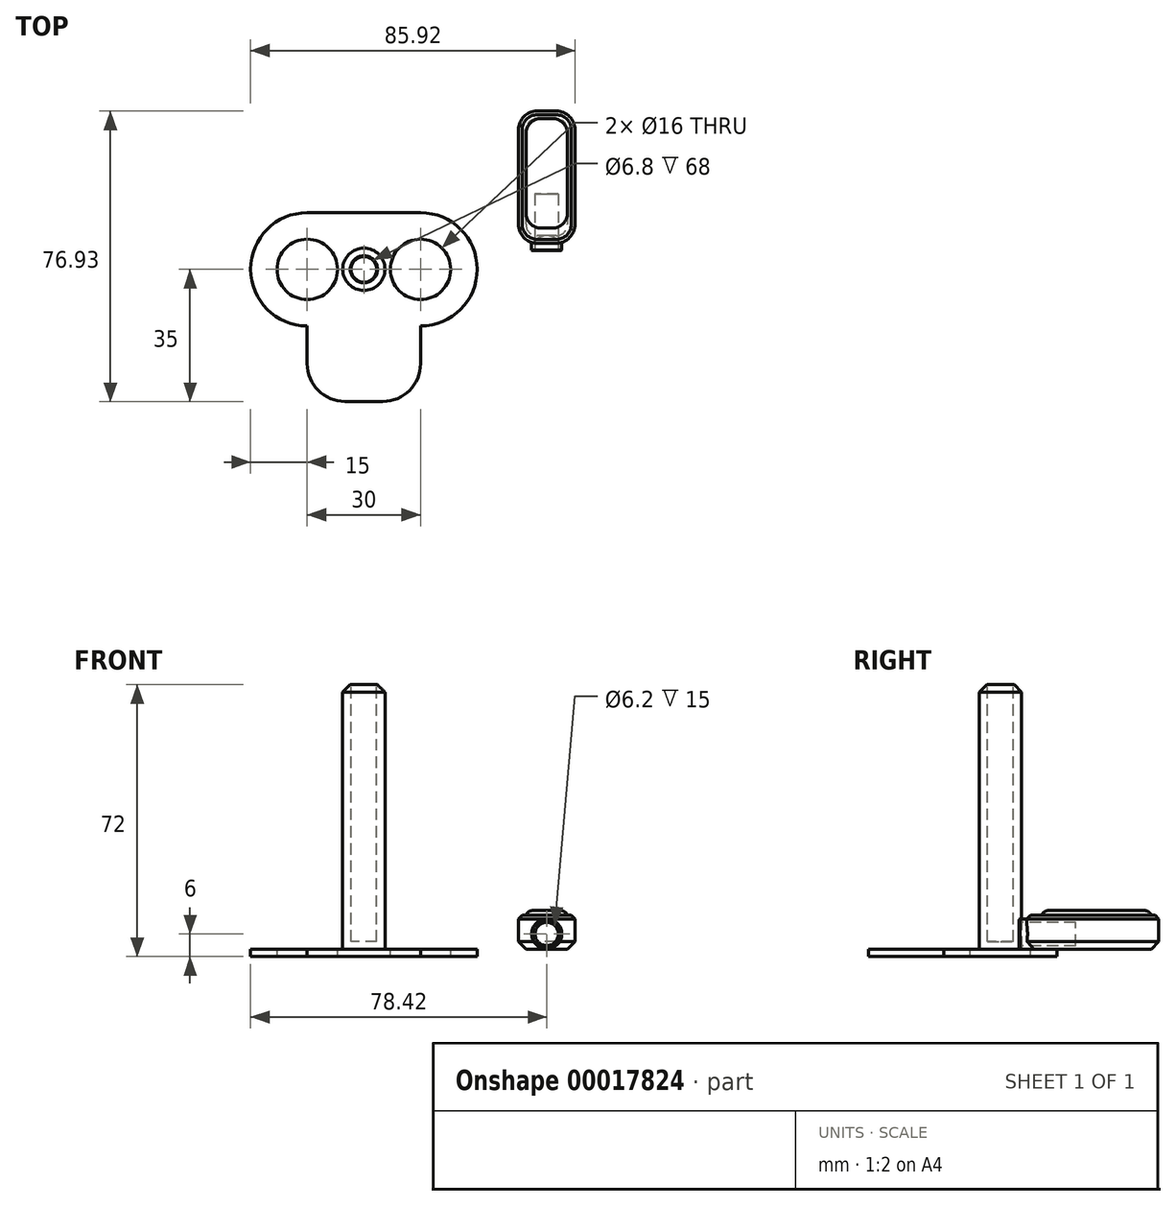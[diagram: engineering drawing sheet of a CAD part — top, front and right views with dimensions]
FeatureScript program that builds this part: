
annotation { "Feature Type Name" : "Feature", "Feature Type Description" : "" }
export const myFeature = defineFeature(function(context is Context, id is Id, definition is map)
    precondition{}
    {
        {
            var Q0;
            Q0=qCreatedBy(makeId("Top.planeOp"),FACE);
            var sketch = newSketch(context, id + "F0", { "sketchPlane" : qUnion([Q0])});
            skCircle(sketch, "E0", {"center": v(0, 0) * mm, "radius": 5.6 * mm});
            skSolve(sketch);
        }
        {
            var Q0;
            Q0 = qSketchRegion(id + "F0", true);
            extrude(context, id + "F1", {"entities" : qUnion([Q0]), "depth" : 70 * mm});
        }
        {
            var Q0;
            Q0=makeQuery(id+"F1.opExtrude","CAP_FACE",FACE,{"disambiguationData":[OSD([sQuery(id+"F0.wireOp",EDGE,"E0")])],"isStart":false});
            var sketch = newSketch(context, id + "F2", { "sketchPlane" : qUnion([Q0])});
            skCircle(sketch, "E1", {"center": v(0, 0) * mm, "radius": 3.4 * mm});
            skSolve(sketch);
        }
        {
            var Q0;
            Q0 = qSketchRegion(id + "F2", true);
            extrude(context, id + "F3", {"entities" : qUnion([Q0]), "operationType" : NewBodyOperationType.REMOVE, "oppositeDirection" : true, "depth" : 68 * mm});
        }
        {
            var Q0;
            Q0=makeQuery(id+"F1.opExtrude","CAP_EDGE",EDGE,{"disambiguationData":[OSD([sQuery(id+"F0.wireOp",EDGE,"E0")])],"isStart":false});
            chamfer(context, id + "F4", {"entities" : qUnion([Q0]), "width" : 2 * mm});
        }
        {
            var Q0;
            Q0=qCreatedBy(makeId("Top.planeOp"),FACE);
            var sketch = newSketch(context, id + "F5", { "sketchPlane" : qUnion([Q0])});
            skLineSegment(sketch, "E2.bottom", {"start": v(-30, 15) * mm, "end": v(30, 15) * mm});
            skLineSegment(sketch, "E2.top", {"start": v(-30, -15) * mm, "end": v(30, -15) * mm});
            skLineSegment(sketch, "E2.left", {"start": v(-30, 15) * mm, "end": v(-30, -15) * mm});
            skLineSegment(sketch, "E2.right", {"start": v(30, 15) * mm, "end": v(30, -15) * mm});
            skPoint(sketch, "E3", {"position": v(-30, 0) * mm});
            skPoint(sketch, "E4", {"position": v(0, 15) * mm});
            skSolve(sketch);
        }
        {
            var Q0;
            Q0 = qSketchRegion(id + "F5", true);
            extrude(context, id + "F6", {"entities" : qUnion([Q0]), "operationType" : NewBodyOperationType.ADD, "oppositeDirection" : true, "depth" : 2 * mm});
        }
        {
            var Q0;
            Q0=makeQuery(id+"F6.opExtrude","SWEPT_EDGE",EDGE,{"disambiguationData":[OSD([sQuery(id+"F5.wireOp",EDGE,"E2.bottom"),sQuery(id+"F5.wireOp",EDGE,"E2.left")])]});
            var Q1;
            Q1=makeQuery(id+"F6.opExtrude","SWEPT_EDGE",EDGE,{"disambiguationData":[OSD([sQuery(id+"F5.wireOp",EDGE,"E2.top"),sQuery(id+"F5.wireOp",EDGE,"E2.left")])]});
            var Q2;
            Q2=makeQuery(id+"F6.opExtrude","SWEPT_EDGE",EDGE,{"disambiguationData":[OSD([sQuery(id+"F5.wireOp",EDGE,"E2.top"),sQuery(id+"F5.wireOp",EDGE,"E2.right")])]});
            var Q3;
            Q3=makeQuery(id+"F6.opExtrude","SWEPT_EDGE",EDGE,{"disambiguationData":[OSD([sQuery(id+"F5.wireOp",EDGE,"E2.bottom"),sQuery(id+"F5.wireOp",EDGE,"E2.right")])]});
            fillet(context, id + "F7", {"entities" : qUnion([Q0, Q1, Q2, Q3]), "radius" : 15 * mm, "tangentPropagation" : true, "allowEdgeOverflow" : false});
        }
        {
            var Q0;
            Q0=qCreatedBy(makeId("Top.planeOp"),FACE);
            var sketch = newSketch(context, id + "F8", { "sketchPlane" : qUnion([Q0])});
            skLineSegment(sketch, "E5.bottom", {"start": v(40.92, 41.93) * mm, "end": v(55.92, 41.93) * mm});
            skLineSegment(sketch, "E5.top", {"start": v(40.92, 6.93) * mm, "end": v(55.92, 6.93) * mm});
            skLineSegment(sketch, "E5.left", {"start": v(40.92, 41.93) * mm, "end": v(40.92, 6.93) * mm});
            skLineSegment(sketch, "E5.right", {"start": v(55.92, 41.93) * mm, "end": v(55.92, 6.93) * mm});
            skSolve(sketch);
        }
        {
            var Q0;
            Q0=makeQuery(id+"F8.imprint","IMPRINT",FACE,{"disambiguationData":[TD([[makeQuery(id+"F8.imprint","IMPRINT",EDGE,{"derivedFrom":sQuery(id+"F8.wireOp",EDGE,"E5.bottom")}),-1.0]])]});
            extrude(context, id + "F9", {"entities" : qUnion([Q0]), "depth" : 9 * mm});
        }
        {
            var Q0;
            Q0=makeQuery(id+"F9.opExtrude","SWEPT_FACE",FACE,{"disambiguationData":[OSD([sQuery(id+"F8.wireOp",EDGE,"E5.top")])]});
            var sketch = newSketch(context, id + "F10", { "sketchPlane" : qUnion([Q0])});
            skCircle(sketch, "E6", {"center": v(48.42, 4) * mm, "radius": 4 * mm});
            skPoint(sketch, "E7", {"position": v(48.42, 9) * mm});
            skSolve(sketch);
        }
        {
            var Q0;
            Q0=makeQuery(id+"F9.opExtrude","CAP_FACE",FACE,{"disambiguationData":[OSD([sQuery(id+"F8.wireOp",EDGE,"E5.bottom"),sQuery(id+"F8.wireOp",EDGE,"E5.top"),sQuery(id+"F8.wireOp",EDGE,"E5.left"),sQuery(id+"F8.wireOp",EDGE,"E5.right")])],"isStart":false});
            var sketch = newSketch(context, id + "F11", { "sketchPlane" : qUnion([Q0])});
            skLineSegment(sketch, "E8.bottom", {"start": v(42.92, 39.93) * mm, "end": v(53.92, 39.93) * mm});
            skLineSegment(sketch, "E8.top", {"start": v(42.92, 10.93) * mm, "end": v(53.92, 10.93) * mm});
            skLineSegment(sketch, "E8.left", {"start": v(42.92, 39.93) * mm, "end": v(42.92, 10.93) * mm});
            skLineSegment(sketch, "E8.right", {"start": v(53.92, 39.93) * mm, "end": v(53.92, 10.93) * mm});
            skSolve(sketch);
        }
        {
            var Q0;
            Q0 = qSketchRegion(id + "F11", true);
            extrude(context, id + "F12", {"entities" : qUnion([Q0]), "operationType" : NewBodyOperationType.ADD, "depth" : 1.2 * mm});
        }
        {
            var Q0;
            Q0=makeQuery(id+"F12.opExtrude","SWEPT_EDGE",EDGE,{"disambiguationData":[OSD([sQuery(id+"F11.wireOp",EDGE,"E8.top"),sQuery(id+"F11.wireOp",EDGE,"E8.right")])]});
            var Q1;
            Q1=makeQuery(id+"F12.opExtrude","SWEPT_EDGE",EDGE,{"disambiguationData":[OSD([sQuery(id+"F11.wireOp",EDGE,"E8.bottom"),sQuery(id+"F11.wireOp",EDGE,"E8.right")])]});
            var Q2;
            Q2=makeQuery(id+"F12.opExtrude","SWEPT_EDGE",EDGE,{"disambiguationData":[OSD([sQuery(id+"F11.wireOp",EDGE,"E8.bottom"),sQuery(id+"F11.wireOp",EDGE,"E8.left")])]});
            var Q3;
            Q3=makeQuery(id+"F12.opExtrude","SWEPT_EDGE",EDGE,{"disambiguationData":[OSD([sQuery(id+"F11.wireOp",EDGE,"E8.top"),sQuery(id+"F11.wireOp",EDGE,"E8.left")])]});
            fillet(context, id + "F13", {"entities" : qUnion([Q0, Q1, Q2, Q3]), "radius" : 4 * mm, "tangentPropagation" : true, "allowEdgeOverflow" : false});
        }
        {
            var Q0;
            Q0=makeQuery(id+"F9.opExtrude","SWEPT_EDGE",EDGE,{"disambiguationData":[OSD([sQuery(id+"F8.wireOp",EDGE,"E5.bottom"),sQuery(id+"F8.wireOp",EDGE,"E5.left")])]});
            var Q1;
            Q1=makeQuery(id+"F9.opExtrude","SWEPT_EDGE",EDGE,{"disambiguationData":[OSD([sQuery(id+"F8.wireOp",EDGE,"E5.top"),sQuery(id+"F8.wireOp",EDGE,"E5.left")])]});
            var Q2;
            Q2=makeQuery(id+"F9.opExtrude","SWEPT_EDGE",EDGE,{"disambiguationData":[OSD([sQuery(id+"F8.wireOp",EDGE,"E5.top"),sQuery(id+"F8.wireOp",EDGE,"E5.right")])]});
            var Q3;
            Q3=makeQuery(id+"F9.opExtrude","SWEPT_EDGE",EDGE,{"disambiguationData":[OSD([sQuery(id+"F8.wireOp",EDGE,"E5.bottom"),sQuery(id+"F8.wireOp",EDGE,"E5.right")])]});
            fillet(context, id + "F14", {"entities" : qUnion([Q0, Q1, Q2, Q3]), "radius" : 5 * mm, "tangentPropagation" : true, "allowEdgeOverflow" : false});
        }
        {
            var Q0;
            Q0=makeQuery(id+"F12.opExtrude","CAP_FACE",FACE,{"disambiguationData":[OSD([sQuery(id+"F11.wireOp",EDGE,"E8.bottom"),sQuery(id+"F11.wireOp",EDGE,"E8.top"),sQuery(id+"F11.wireOp",EDGE,"E8.left"),sQuery(id+"F11.wireOp",EDGE,"E8.right")])],"isStart":false});
            fillet(context, id + "F15", {"entities" : qUnion([Q0]), "radius" : 2 * mm, "tangentPropagation" : true, "allowEdgeOverflow" : false});
        }
        {
            var Q0;
            Q0=makeQuery(id+"F9.opExtrude","CAP_FACE",FACE,{"disambiguationData":[OSD([sQuery(id+"F8.wireOp",EDGE,"E5.bottom"),sQuery(id+"F8.wireOp",EDGE,"E5.top"),sQuery(id+"F8.wireOp",EDGE,"E5.left"),sQuery(id+"F8.wireOp",EDGE,"E5.right")])],"isStart":true});
            chamfer(context, id + "F16", {"entities" : qUnion([Q0]), "width" : 2 * mm, "tangentPropagation" : true});
        }
        {
            var Q0;
            Q0=makeQuery(id+"F9.opExtrude","CAP_EDGE",EDGE,{"disambiguationData":[OSD([sQuery(id+"F8.wireOp",EDGE,"E5.left")])],"isStart":false});
            chamfer(context, id + "F17", {"entities" : qUnion([Q0]), "width" : 1 * mm, "tangentPropagation" : true});
        }
        {
            var Q0;
            {var subQ2=sQuery(id+"F10.wireOp",EDGE,"E6");Q0=makeQuery(id+"F10.imprint","IMPRINT",FACE,{"disambiguationData":[TD([[makeQuery(id+"F10.imprint","IMPRINT",EDGE,{"derivedFrom":subQ2}),-1.0]])]});}
            cPlane(context, id + "F18", {"entities" : qUnion([Q0]), "cplaneType" : CPlaneType.OFFSET, "offset" : 2 * mm, "width" : 150 * mm, "height" : 150 * mm});
        }
        {
            var Q0;
            Q0=qCreatedBy(id+"F18.planeOp",FACE);
            var sketch = newSketch(context, id + "F19", { "sketchPlane" : qUnion([Q0])});
            skCircle(sketch, "E9", {"center": v(48.42, 4) * mm, "radius": 4 * mm});
            skSolve(sketch);
        }
        {
            var Q0;
            Q0 = qSketchRegion(id + "F19", true);
            extrude(context, id + "F20", {"entities" : qUnion([Q0]), "operationType" : NewBodyOperationType.ADD, "oppositeDirection" : true, "depth" : 10 * mm});
        }
        {
            var Q0;
            Q0=makeQuery(id+"F20.opExtrude","CAP_FACE",FACE,{"disambiguationData":[OSD([sQuery(id+"F19.wireOp",EDGE,"E9")])],"isStart":true});
            var sketch = newSketch(context, id + "F21", { "sketchPlane" : qUnion([Q0])});
            skCircle(sketch, "E10", {"center": v(48.42, 4) * mm, "radius": 3.1 * mm});
            skSolve(sketch);
        }
        {
            var Q0;
            Q0 = qSketchRegion(id + "F21", true);
            extrude(context, id + "F22", {"entities" : qUnion([Q0]), "operationType" : NewBodyOperationType.REMOVE, "oppositeDirection" : true, "depth" : 15 * mm});
        }
        {
            var Q0;
            Q0=makeQuery(id+"F20.opExtrude","CAP_EDGE",EDGE,{"disambiguationData":[OSD([sQuery(id+"F19.wireOp",EDGE,"E9")])],"isStart":true});
            chamfer(context, id + "F23", {"entities" : qUnion([Q0]), "width" : 0.2 * mm, "tangentPropagation" : true});
        }
        {
            var Q0;
            Q0=makeQuery(id+"F6.opExtrude","CAP_FACE",FACE,{"disambiguationData":[OSD([sQuery(id+"F5.wireOp",EDGE,"E2.bottom"),sQuery(id+"F5.wireOp",EDGE,"E2.top"),sQuery(id+"F5.wireOp",EDGE,"E2.left"),sQuery(id+"F5.wireOp",EDGE,"E2.right")])],"isStart":true});
            var sketch = newSketch(context, id + "F24", { "sketchPlane" : qUnion([Q0])});
            skCircle(sketch, "E11", {"center": v(-15, 0) * mm, "radius": 8 * mm});
            skCircle(sketch, "E12", {"center": v(15, 0) * mm, "radius": 8 * mm});
            skSolve(sketch);
        }
        {
            var Q0;
            Q0 = qSketchRegion(id + "F24", true);
            extrude(context, id + "F25", {"entities" : qUnion([Q0]), "operationType" : NewBodyOperationType.REMOVE, "endBound" : BoundingType.THROUGH_ALL, "oppositeDirection" : true, "depth" : 25 * mm});
        }
        {
            var Q0;
            Q0=makeQuery(id+"F6.opExtrude","CAP_FACE",FACE,{"disambiguationData":[OSD([sQuery(id+"F5.wireOp",EDGE,"E2.bottom"),sQuery(id+"F5.wireOp",EDGE,"E2.top"),sQuery(id+"F5.wireOp",EDGE,"E2.left"),sQuery(id+"F5.wireOp",EDGE,"E2.right")])],"isStart":true});
            var sketch = newSketch(context, id + "F26", { "sketchPlane" : qUnion([Q0])});
            skLineSegment(sketch, "E13.bottom", {"start": v(-15, -15) * mm, "end": v(15, -15) * mm});
            skLineSegment(sketch, "E13.top", {"start": v(-15, -35) * mm, "end": v(15, -35) * mm});
            skLineSegment(sketch, "E13.left", {"start": v(-15, -15) * mm, "end": v(-15, -35) * mm});
            skLineSegment(sketch, "E13.right", {"start": v(15, -15) * mm, "end": v(15, -35) * mm});
            skSolve(sketch);
        }
        {
            var Q0;
            Q0 = qSketchRegion(id + "F26", true);
            var Q1;
            Q1=makeQuery(id+"F6.opExtrude","CAP_FACE",FACE,{"disambiguationData":[OSD([sQuery(id+"F5.wireOp",EDGE,"E2.bottom"),sQuery(id+"F5.wireOp",EDGE,"E2.top"),sQuery(id+"F5.wireOp",EDGE,"E2.left"),sQuery(id+"F5.wireOp",EDGE,"E2.right")])],"isStart":false});
            extrude(context, id + "F27", {"entities" : qUnion([Q0]), "operationType" : NewBodyOperationType.ADD, "endBound" : BoundingType.UP_TO_SURFACE, "oppositeDirection" : true, "endBoundEntityFace" : qUnion([Q1]), "depth" : 25 * mm});
        }
        {
            var Q0;
            Q0=makeQuery(id+"F27.opExtrude","SWEPT_EDGE",EDGE,{"disambiguationData":[OSD([sQuery(id+"F26.wireOp",EDGE,"E13.top"),sQuery(id+"F26.wireOp",EDGE,"E13.left")])]});
            var Q1;
            Q1=makeQuery(id+"F27.opExtrude","SWEPT_EDGE",EDGE,{"disambiguationData":[OSD([sQuery(id+"F26.wireOp",EDGE,"E13.top"),sQuery(id+"F26.wireOp",EDGE,"E13.right")])]});
            fillet(context, id + "F28", {"entities" : qUnion([Q0, Q1]), "radius" : 10 * mm, "tangentPropagation" : true, "allowEdgeOverflow" : false});
        }
    });
